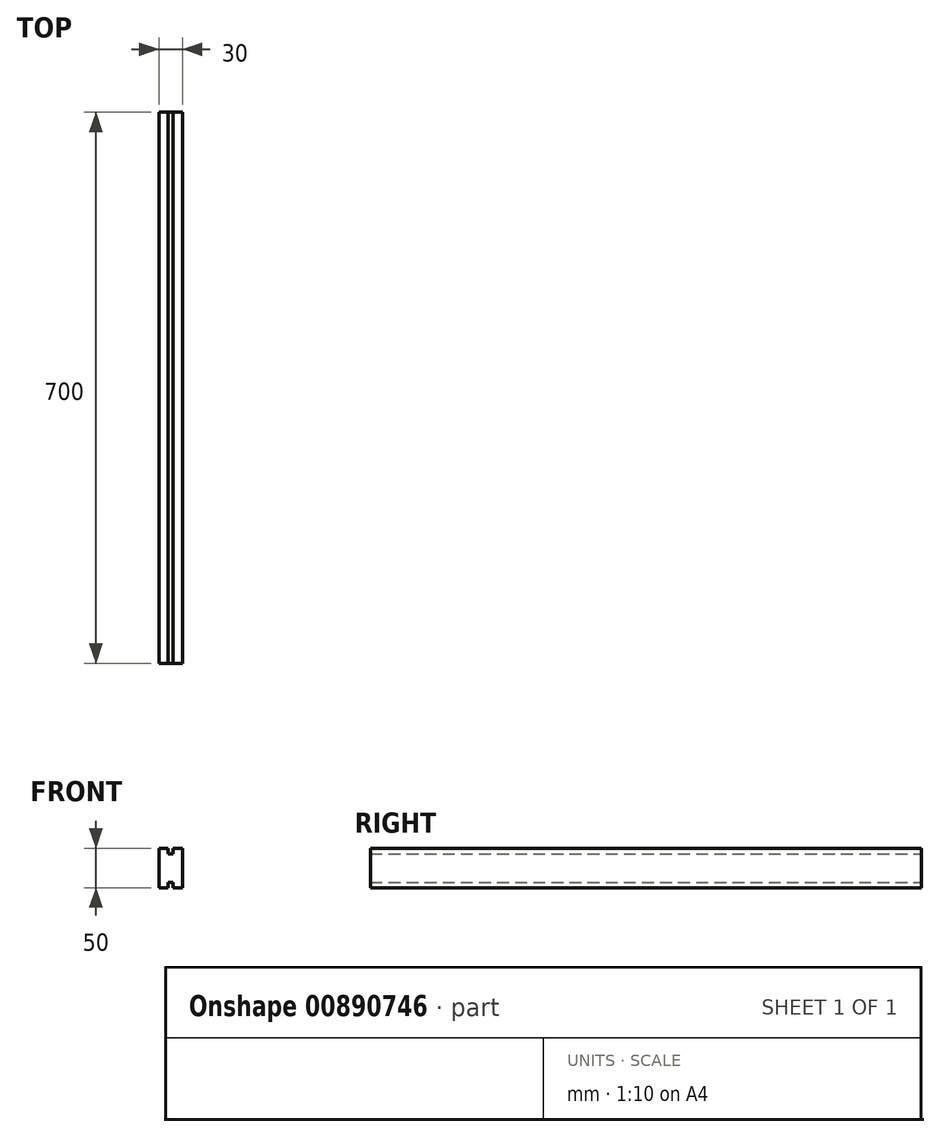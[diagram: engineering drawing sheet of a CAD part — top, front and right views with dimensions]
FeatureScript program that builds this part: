
annotation { "Feature Type Name" : "Feature", "Feature Type Description" : "" }
export const myFeature = defineFeature(function(context is Context, id is Id, definition is map)
    precondition{}
    {
        {
            var Q0;
            Q0=qCreatedBy(makeId("Front.planeOp"),FACE);
            var sketch = newSketch(context, id + "F0", { "sketchPlane" : qUnion([Q0])});
            skLineSegment(sketch, "E0", {"start": v(-47.68, 22.98) * mm, "end": v(-47.68, -27.02) * mm});
            skPoint(sketch, "E1", {"position": v(-32.68, -27.02) * mm});
            skPoint(sketch, "E2", {"position": v(-35.93, -27.02) * mm});
            skPoint(sketch, "E3", {"position": v(-29.43, -27.02) * mm});
            skPoint(sketch, "E4", {"position": v(-17.68, -27.02) * mm});
            skLineSegment(sketch, "E5", {"start": v(-47.68, -27.02) * mm, "end": v(-35.93, -27.02) * mm});
            skLineSegment(sketch, "E6", {"start": v(-35.93, -27.02) * mm, "end": v(-35.93, -20.02) * mm});
            skLineSegment(sketch, "E7", {"start": v(-35.93, -20.02) * mm, "end": v(-29.43, -20.02) * mm});
            skLineSegment(sketch, "E8", {"start": v(-29.43, -20.02) * mm, "end": v(-29.43, -27.02) * mm});
            skLineSegment(sketch, "E9", {"start": v(-17.68, -27.02) * mm, "end": v(-29.43, -27.02) * mm});
            skLineSegment(sketch, "E10", {"start": v(-17.68, -27.02) * mm, "end": v(-17.68, 22.98) * mm});
            skPoint(sketch, "E11", {"position": v(-32.68, 22.98) * mm});
            skPoint(sketch, "E12", {"position": v(-35.93, 22.98) * mm});
            skPoint(sketch, "E13", {"position": v(-29.43, 22.98) * mm});
            skLineSegment(sketch, "E14", {"start": v(-47.68, 22.98) * mm, "end": v(-35.93, 22.98) * mm});
            skLineSegment(sketch, "E15", {"start": v(-35.93, 22.98) * mm, "end": v(-35.93, 15.98) * mm});
            skLineSegment(sketch, "E16", {"start": v(-29.43, 15.98) * mm, "end": v(-35.93, 15.98) * mm});
            skLineSegment(sketch, "E17", {"start": v(-29.43, 15.98) * mm, "end": v(-29.43, 22.98) * mm});
            skLineSegment(sketch, "E18", {"start": v(-29.43, 22.98) * mm, "end": v(-17.68, 22.98) * mm});
            skSolve(sketch);
        }
        {
            var Q0;
            Q0=makeQuery(id+"F0.imprint","IMPRINT",FACE,{"disambiguationData":[TD([[makeQuery(id+"F0.imprint","IMPRINT",EDGE,{"derivedFrom":sQuery(id+"F0.wireOp",EDGE,"E0")}),1.0]])]});
            extrude(context, id + "F1", {"entities" : qUnion([Q0]), "depth" : 700 * mm, "offsetDistance" : 25 * mm});
        }
    });
